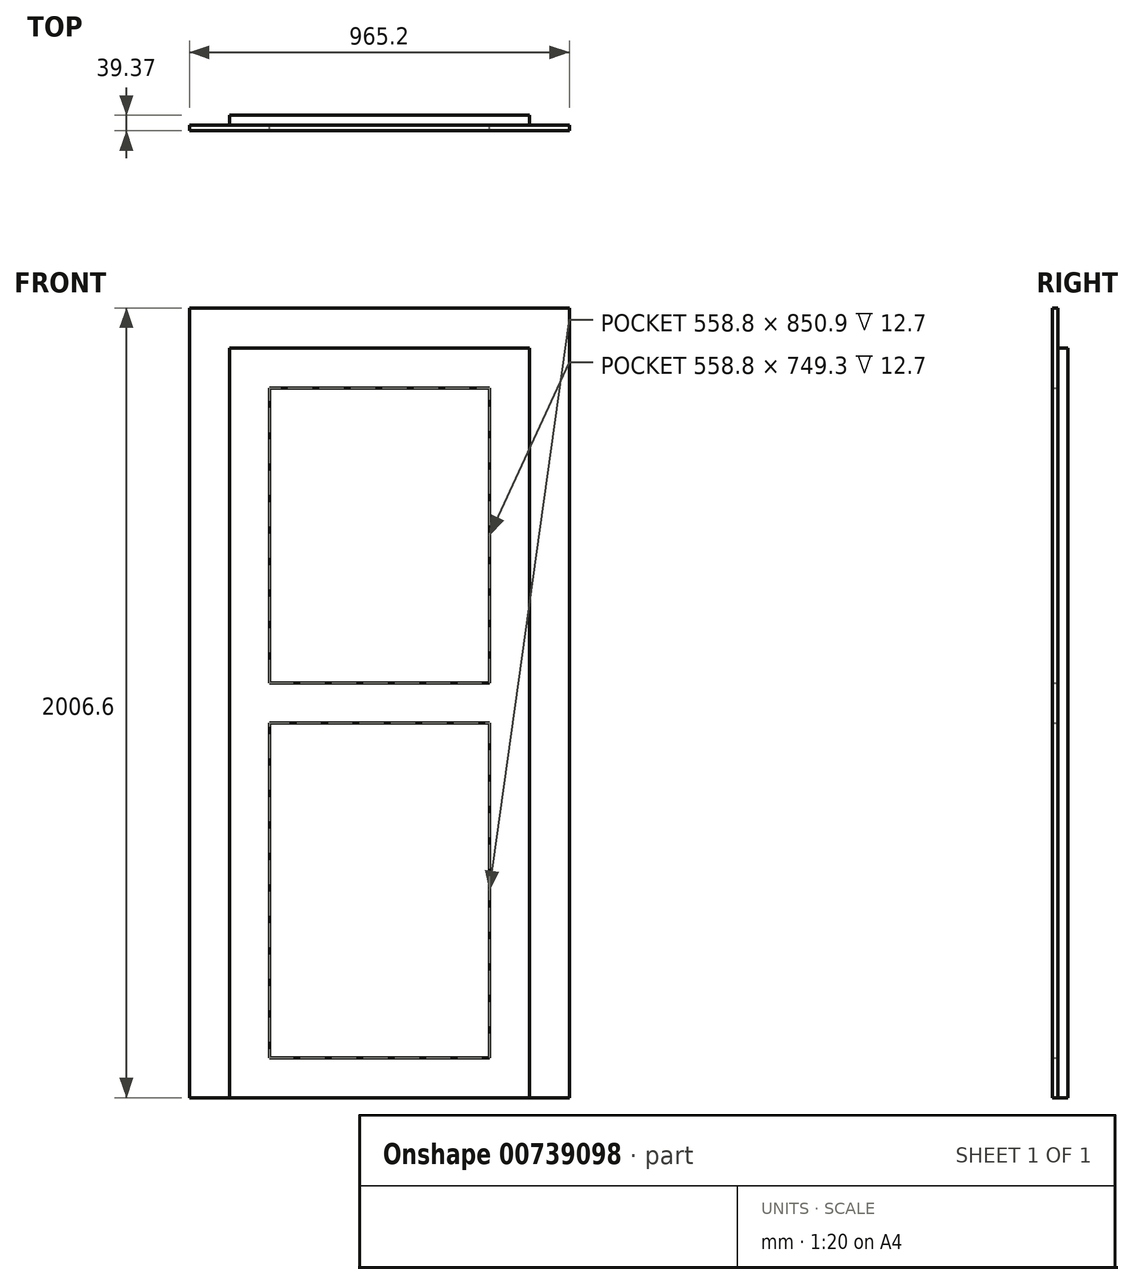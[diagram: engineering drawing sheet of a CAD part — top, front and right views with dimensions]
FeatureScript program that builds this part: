
annotation { "Feature Type Name" : "Feature", "Feature Type Description" : "" }
export const myFeature = defineFeature(function(context is Context, id is Id, definition is map)
    precondition{}
    {
        {
            var Q0;
            Q0=qCreatedBy(makeId("Front.planeOp"),FACE);
            var sketch = newSketch(context, id + "F0", { "sketchPlane" : qUnion([Q0])});
            skLineSegment(sketch, "E0.bottom", {"start": v(0, 0) * mm, "end": v(762, 0) * mm});
            skLineSegment(sketch, "E0.top", {"start": v(0, 1905) * mm, "end": v(762, 1905) * mm});
            skLineSegment(sketch, "E0.left", {"start": v(0, 0) * mm, "end": v(0, 1905) * mm});
            skLineSegment(sketch, "E0.right", {"start": v(762, 0) * mm, "end": v(762, 1905) * mm});
            skLineSegment(sketch, "E1.0", {"start": v(101.6, 101.6) * mm, "end": v(101.6, 952.5) * mm});
            skLineSegment(sketch, "E1.1", {"start": v(101.6, 101.6) * mm, "end": v(660.4, 101.6) * mm});
            skLineSegment(sketch, "E1.2", {"start": v(660.4, 101.6) * mm, "end": v(660.4, 952.5) * mm});
            skLineSegment(sketch, "E1.3", {"start": v(101.6, 1803.4) * mm, "end": v(660.4, 1803.4) * mm});
            skLineSegment(sketch, "E2.0", {"start": v(101.6, 952.5) * mm, "end": v(660.4, 952.5) * mm});
            skLineSegment(sketch, "E3.0", {"start": v(101.6, 1054.1) * mm, "end": v(660.4, 1054.1) * mm});
            skPoint(sketch, "E4.end.orphan", {"position": v(660.4, 952.5) * mm});
            skPoint(sketch, "E4.start.orphan", {"position": v(101.6, 952.5) * mm});
            skLineSegment(sketch, "E5.trimOffspring", {"start": v(101.6, 1054.1) * mm, "end": v(101.6, 1803.4) * mm});
            skLineSegment(sketch, "E6.trimOffspring", {"start": v(660.4, 1054.1) * mm, "end": v(660.4, 1803.4) * mm});
            skSolve(sketch);
        }
        {
            var Q0;
            Q0=makeQuery(id+"F0.imprint","IMPRINT",FACE,{"disambiguationData":[TD([[makeQuery(id+"F0.imprint","IMPRINT",EDGE,{"derivedFrom":sQuery(id+"F0.wireOp",EDGE,"E0.bottom")}),1.0]])]});
            extrude(context, id + "F1", {"entities" : qUnion([Q0]), "depth" : 12.7 * mm, "offsetDistance" : 25.4 * mm});
        }
        {
            var Q0;
            Q0=makeQuery(id+"F1.opExtrude","CAP_FACE",FACE,{"disambiguationData":[OSD([sQuery(id+"F0.wireOp",EDGE,"E0.bottom"),sQuery(id+"F0.wireOp",EDGE,"E0.top"),sQuery(id+"F0.wireOp",EDGE,"E0.left"),sQuery(id+"F0.wireOp",EDGE,"E0.right"),sQuery(id+"F0.wireOp",EDGE,"E1.0"),sQuery(id+"F0.wireOp",EDGE,"E1.1"),sQuery(id+"F0.wireOp",EDGE,"E1.2"),sQuery(id+"F0.wireOp",EDGE,"E1.3"),sQuery(id+"F0.wireOp",EDGE,"E2.0"),sQuery(id+"F0.wireOp",EDGE,"E3.0"),sQuery(id+"F0.wireOp",EDGE,"E5.trimOffspring"),sQuery(id+"F0.wireOp",EDGE,"E6.trimOffspring")])],"isStart":true});
            var sketch = newSketch(context, id + "F2", { "sketchPlane" : qUnion([Q0])});
            skLineSegment(sketch, "E7", {"start": v(0, 0) * mm, "end": v(101.6, 0) * mm});
            skLineSegment(sketch, "E8", {"start": v(101.6, 0) * mm, "end": v(101.6, 2006.6) * mm});
            skLineSegment(sketch, "E9", {"start": v(101.6, 2006.6) * mm, "end": v(-863.6, 2006.6) * mm});
            skLineSegment(sketch, "E10", {"start": v(-863.6, 2006.6) * mm, "end": v(-863.6, 0) * mm});
            skLineSegment(sketch, "E11", {"start": v(-863.6, 0) * mm, "end": v(-762, 0) * mm});
            skLineSegment(sketch, "E12", {"start": v(-762, 0) * mm, "end": v(-762, 1905) * mm});
            skLineSegment(sketch, "E13", {"start": v(-762, 1905) * mm, "end": v(0, 1905) * mm});
            skLineSegment(sketch, "E14", {"start": v(0, 1905) * mm, "end": v(0, 0) * mm});
            skSolve(sketch);
        }
        {
            var Q0;
            Q0=makeQuery(id+"F2.imprint","IMPRINT",FACE,{"disambiguationData":[TD([[makeQuery(id+"F2.imprint","IMPRINT",EDGE,{"derivedFrom":sQuery(id+"F2.wireOp",EDGE,"E7")}),1.0]])]});
            extrude(context, id + "F3", {"entities" : qUnion([Q0]), "operationType" : NewBodyOperationType.ADD, "oppositeDirection" : true, "depth" : 13.97 * mm, "offsetDistance" : 25.4 * mm});
        }
        {
            var Q0;
            Q0=makeQuery(id+"F3.boolean.opBoolean","MERGE",FACE,{"derivedFrom":[makeQuery(id+"F1.opExtrude","CAP_FACE",FACE,{"disambiguationData":[OSD([sQuery(id+"F0.wireOp",EDGE,"E0.bottom"),sQuery(id+"F0.wireOp",EDGE,"E0.top"),sQuery(id+"F0.wireOp",EDGE,"E0.left"),sQuery(id+"F0.wireOp",EDGE,"E0.right"),sQuery(id+"F0.wireOp",EDGE,"E1.0"),sQuery(id+"F0.wireOp",EDGE,"E1.1"),sQuery(id+"F0.wireOp",EDGE,"E1.2"),sQuery(id+"F0.wireOp",EDGE,"E1.3"),sQuery(id+"F0.wireOp",EDGE,"E2.0"),sQuery(id+"F0.wireOp",EDGE,"E3.0"),sQuery(id+"F0.wireOp",EDGE,"E5.trimOffspring"),sQuery(id+"F0.wireOp",EDGE,"E6.trimOffspring")])],"isStart":true}),makeQuery(id+"F3.opExtrude","CAP_FACE",FACE,{"disambiguationData":[OSD([sQuery(id+"F2.wireOp",EDGE,"E7"),sQuery(id+"F2.wireOp",EDGE,"E8"),sQuery(id+"F2.wireOp",EDGE,"E9"),sQuery(id+"F2.wireOp",EDGE,"E10"),sQuery(id+"F2.wireOp",EDGE,"E11"),sQuery(id+"F2.wireOp",EDGE,"E12"),sQuery(id+"F2.wireOp",EDGE,"E13"),sQuery(id+"F2.wireOp",EDGE,"E14")])],"isStart":true})]});
            var sketch = newSketch(context, id + "F4", { "sketchPlane" : qUnion([Q0])});
            skLineSegment(sketch, "E15.0", {"start": v(-762, 0) * mm, "end": v(-762, 1905) * mm});
            skLineSegment(sketch, "E16.0", {"start": v(0, 0) * mm, "end": v(0, 1905) * mm});
            skLineSegment(sketch, "E17", {"start": v(-762, 1905) * mm, "end": v(0, 1905) * mm});
            skLineSegment(sketch, "E18", {"start": v(-762, 0) * mm, "end": v(0, 0) * mm});
            skSolve(sketch);
        }
        {
            var Q0;
            Q0 = qSketchRegion(id + "F4", true);
            extrude(context, id + "F5", {"entities" : qUnion([Q0]), "operationType" : NewBodyOperationType.ADD, "depth" : 25.4 * mm, "offsetDistance" : 25.4 * mm});
        }
    });
